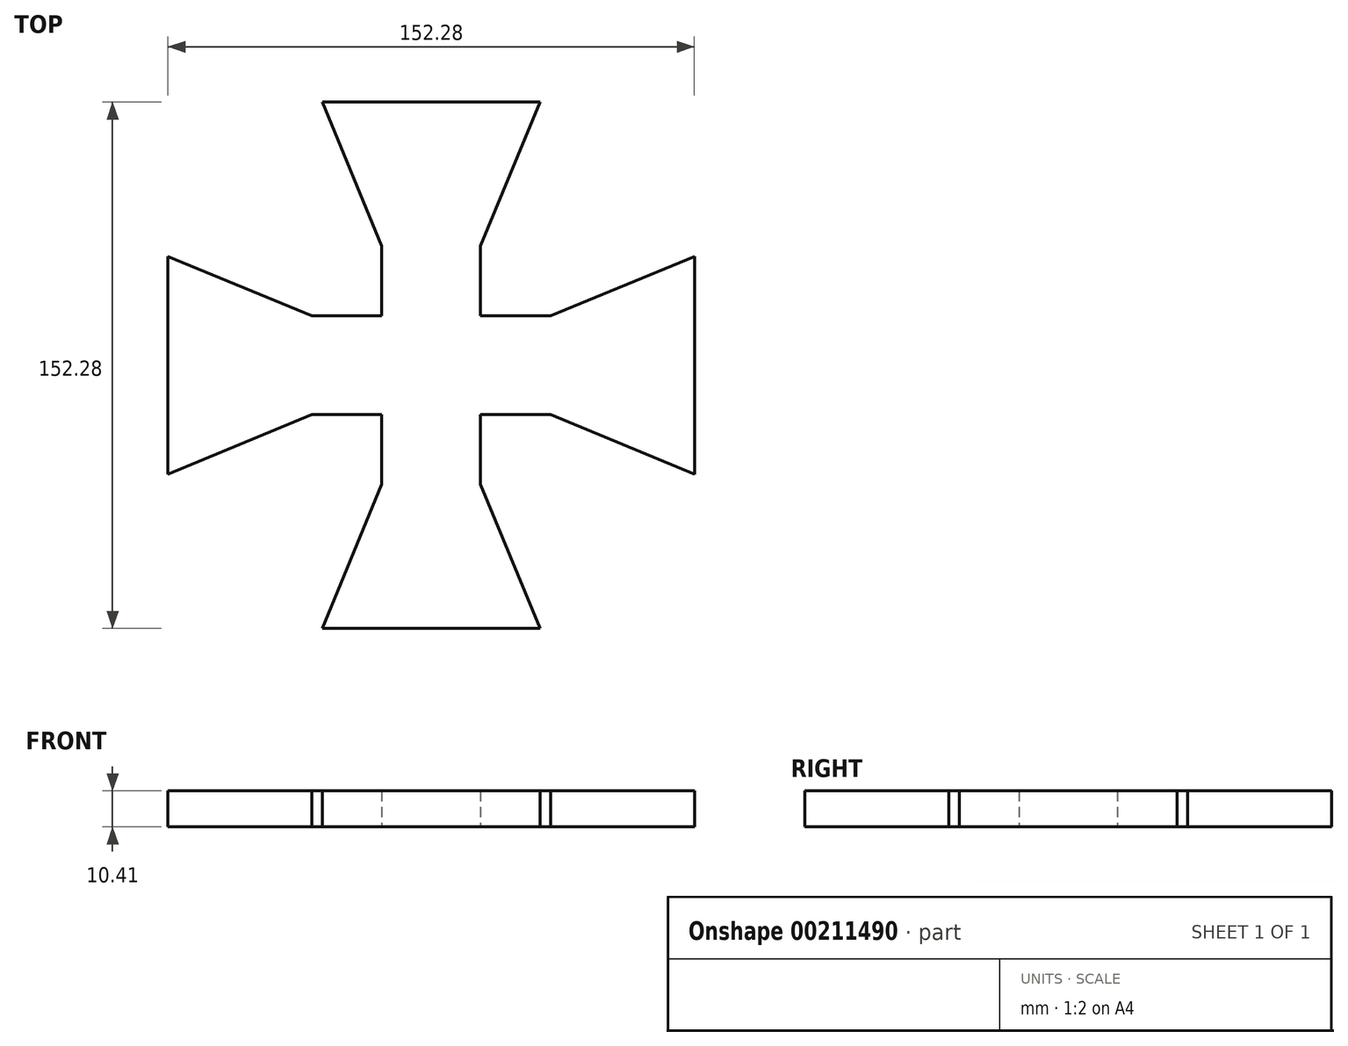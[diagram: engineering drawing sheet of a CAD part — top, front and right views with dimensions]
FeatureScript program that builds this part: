
annotation { "Feature Type Name" : "Feature", "Feature Type Description" : "" }
export const myFeature = defineFeature(function(context is Context, id is Id, definition is map)
    precondition{}
    {
        {
            var Q0;
            Q0=qCreatedBy(makeId("Top.planeOp"),FACE);
            var sketch = newSketch(context, id + "F0", { "sketchPlane" : qUnion([Q0])});
            skLineSegment(sketch, "E0.0", {"start": v(-31.54, 76.14) * mm, "end": v(31.54, 76.14) * mm});
            skLineSegment(sketch, "E0.2", {"start": v(76.14, 31.54) * mm, "end": v(76.14, -31.54) * mm});
            skLineSegment(sketch, "E0.4", {"start": v(31.54, -76.14) * mm, "end": v(-31.54, -76.14) * mm});
            skLineSegment(sketch, "E0.6", {"start": v(-76.14, -31.54) * mm, "end": v(-76.14, 31.54) * mm});
            skPoint(sketch, "E0.0.midPoint", {"position": v(0, 76.14) * mm});
            skPoint(sketch, "E1.0.midPoint", {"position": v(0, 34.49) * mm});
            skLineSegment(sketch, "E2", {"start": v(-31.54, 76.14) * mm, "end": v(-14.29, 34.49) * mm});
            skLineSegment(sketch, "E3", {"start": v(14.29, 34.49) * mm, "end": v(31.54, 76.14) * mm});
            skLineSegment(sketch, "E4", {"start": v(-34.49, 14.29) * mm, "end": v(-76.14, 31.54) * mm});
            skLineSegment(sketch, "E5", {"start": v(-76.14, -31.54) * mm, "end": v(-34.49, -14.29) * mm});
            skLineSegment(sketch, "E6", {"start": v(-14.29, -34.49) * mm, "end": v(-31.54, -76.14) * mm});
            skLineSegment(sketch, "E7", {"start": v(14.29, -34.49) * mm, "end": v(31.54, -76.14) * mm});
            skLineSegment(sketch, "E8", {"start": v(34.49, -14.29) * mm, "end": v(76.14, -31.54) * mm});
            skLineSegment(sketch, "E9", {"start": v(34.49, 14.29) * mm, "end": v(76.14, 31.54) * mm});
            skLineSegment(sketch, "E10", {"start": v(-14.29, 14.29) * mm, "end": v(-14.29, 34.49) * mm});
            skLineSegment(sketch, "E11", {"start": v(-34.49, 14.29) * mm, "end": v(-14.29, 14.29) * mm});
            skLineSegment(sketch, "E12", {"start": v(14.29, 34.49) * mm, "end": v(14.29, 14.29) * mm});
            skLineSegment(sketch, "E13", {"start": v(14.29, 14.29) * mm, "end": v(34.49, 14.29) * mm});
            skLineSegment(sketch, "E14", {"start": v(34.49, -14.29) * mm, "end": v(14.29, -14.29) * mm});
            skLineSegment(sketch, "E15", {"start": v(14.29, -14.29) * mm, "end": v(14.29, -34.49) * mm});
            skLineSegment(sketch, "E16", {"start": v(-14.29, -34.49) * mm, "end": v(-14.29, -14.29) * mm});
            skLineSegment(sketch, "E17", {"start": v(-14.29, -14.29) * mm, "end": v(-34.49, -14.29) * mm});
            skSolve(sketch);
        }
        {
            var Q0;
            Q0 = qSketchRegion(id + "F0", true);
            extrude(context, id + "F1", {"entities" : qUnion([Q0]), "depth" : 10.4 * mm});
        }
    });
